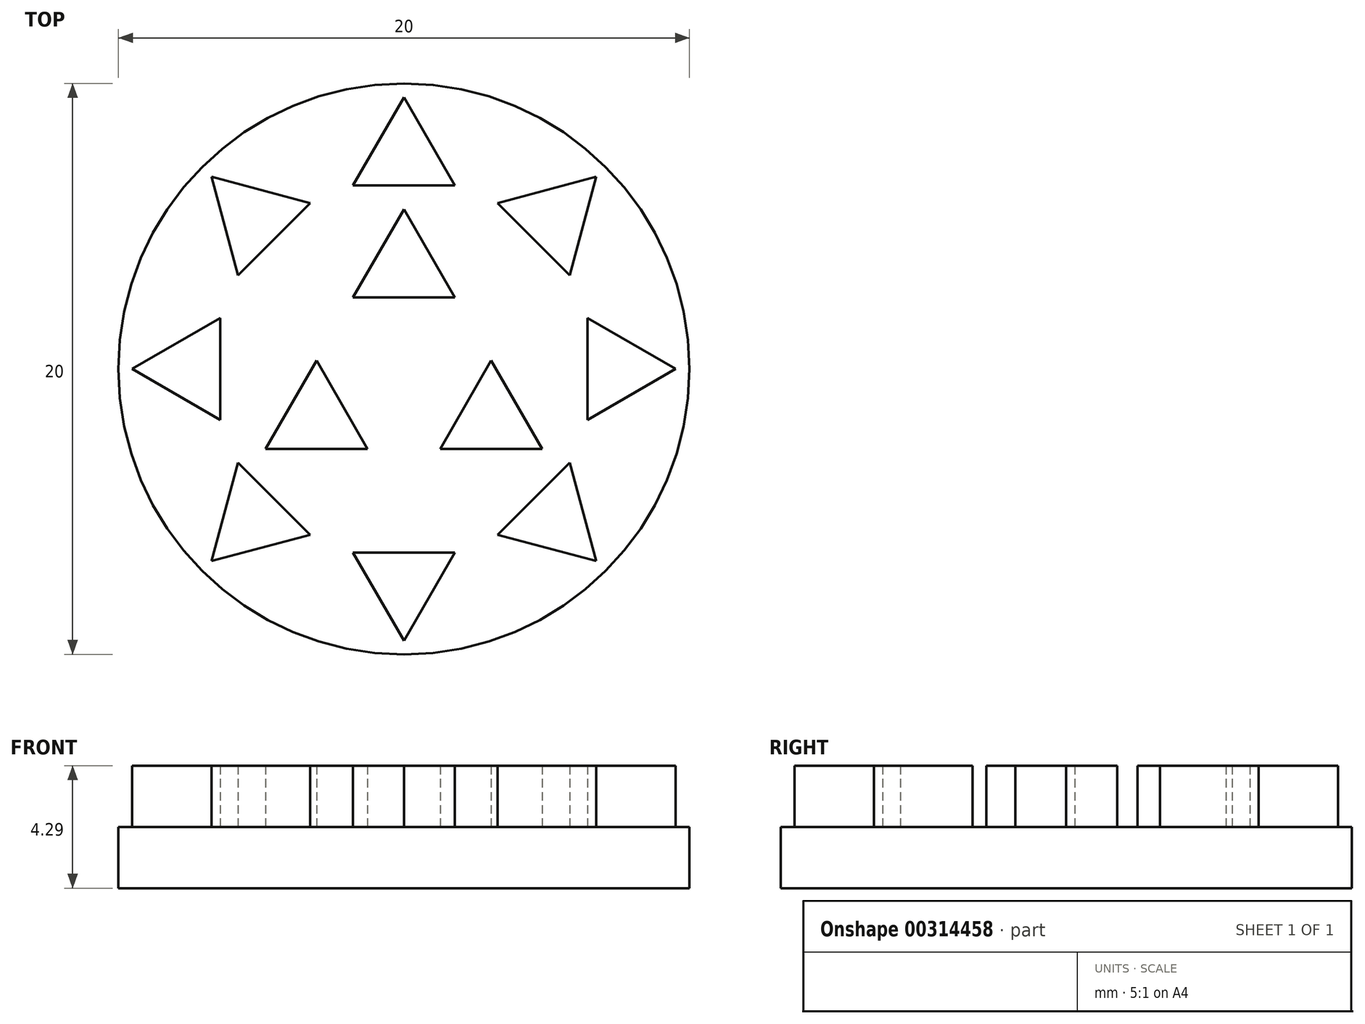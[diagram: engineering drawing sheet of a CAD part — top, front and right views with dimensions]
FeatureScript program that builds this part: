
annotation { "Feature Type Name" : "Feature", "Feature Type Description" : "" }
export const myFeature = defineFeature(function(context is Context, id is Id, definition is map)
    precondition{}
    {
        {
            var Q0;
            Q0=qCreatedBy(makeId("Top.planeOp"),FACE);
            var sketch = newSketch(context, id + "F0", { "sketchPlane" : qUnion([Q0])});
            skCircle(sketch, "E0", {"center": v(0, 0) * mm, "radius": 14 * mm});
            skSolve(sketch);
        }
        {
            var Q0;
            Q0=makeQuery(id+"F0.imprint","IMPRINT",FACE,{"disambiguationData":[TD([[makeQuery(id+"F0.imprint","IMPRINT",EDGE,{"derivedFrom":sQuery(id+"F0.wireOp",EDGE,"E0")}),1.0]])]});
            var Q1;
            Q1 = qSketchRegion(id + "F2", true);
            extrude(context, id + "F1", {"entities" : qUnion([Q0, Q1]), "depth" : 3 * mm});
        }
        {
            var Q0;
            Q0=makeQuery(id+"F1.opExtrude","CAP_FACE",FACE,{"disambiguationData":[OSD([sQuery(id+"F0.wireOp",EDGE,"E0")])],"isStart":false});
            var sketch = newSketch(context, id + "F2", { "sketchPlane" : qUnion([Q0])});
            skCircle(sketch, "E1.cCircle", {"center": v(0, 4.94) * mm, "radius": 1.44 * mm, "construction": true});
            skLineSegment(sketch, "E1.0", {"start": v(2.5, 3.5) * mm, "end": v(-2.5, 3.5) * mm});
            skLineSegment(sketch, "E1.1", {"start": v(-2.5, 3.5) * mm, "end": v(0, 7.83) * mm});
            skLineSegment(sketch, "E1.2", {"start": v(0, 7.83) * mm, "end": v(2.5, 3.5) * mm});
            skPoint(sketch, "E1.0.midPoint", {"position": v(0, 3.5) * mm});
            skCircle(sketch, "E2", {"center": v(0, 0) * mm, "radius": 3.5 * mm});
            skLineSegment(sketch, "E3.1.0", {"start": v(-4.28, 0.42) * mm, "end": v(-1.78, -3.92) * mm});
            skLineSegment(sketch, "E3.1.1", {"start": v(-6.78, -3.92) * mm, "end": v(-4.28, 0.42) * mm});
            skLineSegment(sketch, "E3.1.2", {"start": v(-1.78, -3.92) * mm, "end": v(-6.78, -3.92) * mm});
            skCircle(sketch, "E3.1.3", {"center": v(-4.28, -2.47) * mm, "radius": 1.44 * mm, "construction": true});
            skLineSegment(sketch, "E3.2.0", {"start": v(1.78, -3.92) * mm, "end": v(4.28, 0.42) * mm});
            skLineSegment(sketch, "E3.2.1", {"start": v(6.78, -3.92) * mm, "end": v(1.78, -3.92) * mm});
            skLineSegment(sketch, "E3.2.2", {"start": v(4.28, 0.42) * mm, "end": v(6.78, -3.92) * mm});
            skCircle(sketch, "E3.2.3", {"center": v(4.28, -2.47) * mm, "radius": 1.44 * mm, "construction": true});
            skCircle(sketch, "E4.cCircle", {"center": v(0, 10.44) * mm, "radius": 1.44 * mm, "construction": true});
            skLineSegment(sketch, "E4.0", {"start": v(2.5, 9) * mm, "end": v(-2.5, 9) * mm});
            skLineSegment(sketch, "E4.1", {"start": v(-2.5, 9) * mm, "end": v(0, 13.33) * mm});
            skLineSegment(sketch, "E4.2", {"start": v(0, 13.33) * mm, "end": v(2.5, 9) * mm});
            skPoint(sketch, "E4.0.midPoint", {"position": v(0, 9) * mm});
            skCircle(sketch, "E5", {"center": v(0, 0) * mm, "radius": 9 * mm});
            skLineSegment(sketch, "E6.1.0", {"start": v(-4.6, 8.13) * mm, "end": v(-8.13, 4.6) * mm});
            skLineSegment(sketch, "E6.1.1", {"start": v(-9.43, 9.43) * mm, "end": v(-4.6, 8.13) * mm});
            skLineSegment(sketch, "E6.1.2", {"start": v(-8.13, 4.6) * mm, "end": v(-9.43, 9.43) * mm});
            skCircle(sketch, "E6.1.3", {"center": v(-7.38, 7.38) * mm, "radius": 1.44 * mm, "construction": true});
            skLineSegment(sketch, "E6.2.0", {"start": v(-9, 2.5) * mm, "end": v(-9, -2.5) * mm});
            skLineSegment(sketch, "E6.2.1", {"start": v(-13.33, 0) * mm, "end": v(-9, 2.5) * mm});
            skLineSegment(sketch, "E6.2.2", {"start": v(-9, -2.5) * mm, "end": v(-13.33, 0) * mm});
            skCircle(sketch, "E6.2.3", {"center": v(-10.44, 0) * mm, "radius": 1.44 * mm, "construction": true});
            skLineSegment(sketch, "E7.2.3.0", {"start": v(-8.13, -4.6) * mm, "end": v(-4.6, -8.13) * mm});
            skLineSegment(sketch, "E7.3.3.0", {"start": v(-9.43, -9.43) * mm, "end": v(-8.13, -4.6) * mm});
            skLineSegment(sketch, "E7.6.3.0", {"start": v(-4.6, -8.13) * mm, "end": v(-9.43, -9.43) * mm});
            skCircle(sketch, "E7.9.3.0", {"center": v(-7.38, -7.38) * mm, "radius": 1.44 * mm, "construction": true});
            skLineSegment(sketch, "E7.2.4.0", {"start": v(-2.5, -9) * mm, "end": v(2.5, -9) * mm});
            skLineSegment(sketch, "E7.3.4.0", {"start": v(0, -13.33) * mm, "end": v(-2.5, -9) * mm});
            skLineSegment(sketch, "E7.6.4.0", {"start": v(2.5, -9) * mm, "end": v(0, -13.33) * mm});
            skCircle(sketch, "E7.9.4.0", {"center": v(0, -10.44) * mm, "radius": 1.44 * mm, "construction": true});
            skLineSegment(sketch, "E7.2.5.0", {"start": v(4.6, -8.13) * mm, "end": v(8.13, -4.6) * mm});
            skLineSegment(sketch, "E7.3.5.0", {"start": v(9.43, -9.43) * mm, "end": v(4.6, -8.13) * mm});
            skLineSegment(sketch, "E7.6.5.0", {"start": v(8.13, -4.6) * mm, "end": v(9.43, -9.43) * mm});
            skCircle(sketch, "E7.9.5.0", {"center": v(7.38, -7.38) * mm, "radius": 1.44 * mm, "construction": true});
            skLineSegment(sketch, "E7.2.6.0", {"start": v(9, -2.5) * mm, "end": v(9, 2.5) * mm});
            skLineSegment(sketch, "E7.3.6.0", {"start": v(13.33, 0) * mm, "end": v(9, -2.5) * mm});
            skLineSegment(sketch, "E7.6.6.0", {"start": v(9, 2.5) * mm, "end": v(13.33, 0) * mm});
            skCircle(sketch, "E7.9.6.0", {"center": v(10.44, 0) * mm, "radius": 1.44 * mm, "construction": true});
            skLineSegment(sketch, "E7.2.7.0", {"start": v(8.13, 4.6) * mm, "end": v(4.6, 8.13) * mm});
            skLineSegment(sketch, "E7.3.7.0", {"start": v(9.43, 9.43) * mm, "end": v(8.13, 4.6) * mm});
            skLineSegment(sketch, "E7.6.7.0", {"start": v(4.6, 8.13) * mm, "end": v(9.43, 9.43) * mm});
            skCircle(sketch, "E7.9.7.0", {"center": v(7.38, 7.38) * mm, "radius": 1.44 * mm, "construction": true});
            skPoint(sketch, "E8", {"position": v(6.36, 6.36) * mm});
            skPoint(sketch, "E9", {"position": v(9, 0) * mm});
            skPoint(sketch, "E10", {"position": v(6.36, -6.36) * mm});
            skPoint(sketch, "E11", {"position": v(0, -9) * mm});
            skPoint(sketch, "E12", {"position": v(-6.36, -6.36) * mm});
            skPoint(sketch, "E13", {"position": v(-9, 0) * mm});
            skPoint(sketch, "E14", {"position": v(-6.36, 6.36) * mm});
            skPoint(sketch, "E15", {"position": v(3.03, -1.75) * mm});
            skPoint(sketch, "E16", {"position": v(-3.03, -1.75) * mm});
            skSolve(sketch);
        }
        {
            var Q0;
            {var subQ3=sQuery(id+"F2.wireOp",EDGE,"8b3eb6cf-7dbc-4c96-a035-3d80c259cfac.1");Q0=makeQuery(id+"F2.imprint","IMPRINT",FACE,{"disambiguationData":[TD([[makeQuery(id+"F2.imprint","IMPRINT",EDGE,{"derivedFrom":subQ3}),-1.0]])]});}
            var Q1;
            {var subQ0=sQuery(id+"F2.wireOp",EDGE,"6c10d993-edd7-4a8d-bda8-a9486d968e1a.5.1");Q1=makeQuery(id+"F2.imprint","IMPRINT",FACE,{"disambiguationData":[TD([[makeQuery(id+"F2.imprint","IMPRINT",EDGE,{"derivedFrom":subQ0}),-1.0]])]});}
            var Q2;
            {var subQ0=sQuery(id+"F2.wireOp",EDGE,"6c10d993-edd7-4a8d-bda8-a9486d968e1a.4.1");Q2=makeQuery(id+"F2.imprint","IMPRINT",FACE,{"disambiguationData":[TD([[makeQuery(id+"F2.imprint","IMPRINT",EDGE,{"derivedFrom":subQ0}),-1.0]])]});}
            var Q3;
            {var subQ0=sQuery(id+"F2.wireOp",EDGE,"6c10d993-edd7-4a8d-bda8-a9486d968e1a.3.1");Q3=makeQuery(id+"F2.imprint","IMPRINT",FACE,{"disambiguationData":[TD([[makeQuery(id+"F2.imprint","IMPRINT",EDGE,{"derivedFrom":subQ0}),-1.0]])]});}
            var Q4;
            {var subQ0=sQuery(id+"F2.wireOp",EDGE,"6c10d993-edd7-4a8d-bda8-a9486d968e1a.2.1");Q4=makeQuery(id+"F2.imprint","IMPRINT",FACE,{"disambiguationData":[TD([[makeQuery(id+"F2.imprint","IMPRINT",EDGE,{"derivedFrom":subQ0}),-1.0]])]});}
            var Q5;
            {var subQ0=sQuery(id+"F2.wireOp",EDGE,"6c10d993-edd7-4a8d-bda8-a9486d968e1a.1.1");Q5=makeQuery(id+"F2.imprint","IMPRINT",FACE,{"disambiguationData":[TD([[makeQuery(id+"F2.imprint","IMPRINT",EDGE,{"derivedFrom":subQ0}),-1.0]])]});}
            var Q6;
            {var subQ0=sQuery(id+"F2.wireOp",EDGE,"947e9cf8-dde9-4160-9a07-f35e782527b7.3.7.0");Q6=makeQuery(id+"F2.imprint","IMPRINT",FACE,{"disambiguationData":[TD([[makeQuery(id+"F2.imprint","IMPRINT",EDGE,{"derivedFrom":subQ0}),-1.0]])]});}
            var Q7;
            {var subQ0=sQuery(id+"F2.wireOp",EDGE,"947e9cf8-dde9-4160-9a07-f35e782527b7.3.6.0");Q7=makeQuery(id+"F2.imprint","IMPRINT",FACE,{"disambiguationData":[TD([[makeQuery(id+"F2.imprint","IMPRINT",EDGE,{"derivedFrom":subQ0}),-1.0]])]});}
            var Q8;
            {var subQ0=sQuery(id+"F2.wireOp",EDGE,"947e9cf8-dde9-4160-9a07-f35e782527b7.11.7.0");Q8=makeQuery(id+"F2.imprint","IMPRINT",FACE,{"disambiguationData":[TD([[makeQuery(id+"F2.imprint","IMPRINT",EDGE,{"derivedFrom":subQ0}),-1.0]])]});}
            var Q9;
            {var subQ0=sQuery(id+"F2.wireOp",EDGE,"E1.1");Q9=makeQuery(id+"F2.imprint","IMPRINT",FACE,{"disambiguationData":[TD([[makeQuery(id+"F2.imprint","IMPRINT",EDGE,{"derivedFrom":subQ0}),-1.0]])]});}
            var Q10;
            {var subQ0=sQuery(id+"F2.wireOp",EDGE,"E1.2");Q10=makeQuery(id+"F2.imprint","IMPRINT",FACE,{"disambiguationData":[TD([[makeQuery(id+"F2.imprint","IMPRINT",EDGE,{"derivedFrom":subQ0}),-1.0]])]});}
            var Q11;
            {var subQ0=sQuery(id+"F2.wireOp",EDGE,"E3.1.1");Q11=makeQuery(id+"F2.imprint","IMPRINT",FACE,{"disambiguationData":[TD([[makeQuery(id+"F2.imprint","IMPRINT",EDGE,{"derivedFrom":subQ0}),-1.0]])]});}
            var Q12;
            {var subQ0=sQuery(id+"F2.wireOp",EDGE,"E3.2.1");Q12=makeQuery(id+"F2.imprint","IMPRINT",FACE,{"disambiguationData":[TD([[makeQuery(id+"F2.imprint","IMPRINT",EDGE,{"derivedFrom":subQ0}),-1.0]])]});}
            var Q13;
            {var subQ0=sQuery(id+"F2.wireOp",EDGE,"78a639ae-5dbe-4d62-8846-17a8c4bbea7f.3.3.0");Q13=makeQuery(id+"F2.imprint","IMPRINT",FACE,{"disambiguationData":[TD([[makeQuery(id+"F2.imprint","IMPRINT",EDGE,{"derivedFrom":subQ0}),-1.0]])]});}
            var Q14;
            {var subQ0=sQuery(id+"F2.wireOp",EDGE,"E6.1.1");Q14=makeQuery(id+"F2.imprint","IMPRINT",FACE,{"disambiguationData":[TD([[makeQuery(id+"F2.imprint","IMPRINT",EDGE,{"derivedFrom":subQ0}),-1.0]])]});}
            var Q15;
            {var subQ3=sQuery(id+"F2.wireOp",EDGE,"E4.1");Q15=makeQuery(id+"F2.imprint","IMPRINT",FACE,{"disambiguationData":[TD([[makeQuery(id+"F2.imprint","IMPRINT",EDGE,{"derivedFrom":subQ3}),-1.0]])]});}
            var Q16;
            {var subQ0=sQuery(id+"F2.wireOp",EDGE,"E7.3.7.0");Q16=makeQuery(id+"F2.imprint","IMPRINT",FACE,{"disambiguationData":[TD([[makeQuery(id+"F2.imprint","IMPRINT",EDGE,{"derivedFrom":subQ0}),-1.0]])]});}
            var Q17;
            {var subQ0=sQuery(id+"F2.wireOp",EDGE,"E7.3.6.0");Q17=makeQuery(id+"F2.imprint","IMPRINT",FACE,{"disambiguationData":[TD([[makeQuery(id+"F2.imprint","IMPRINT",EDGE,{"derivedFrom":subQ0}),-1.0]])]});}
            var Q18;
            {var subQ0=sQuery(id+"F2.wireOp",EDGE,"E7.3.5.0");Q18=makeQuery(id+"F2.imprint","IMPRINT",FACE,{"disambiguationData":[TD([[makeQuery(id+"F2.imprint","IMPRINT",EDGE,{"derivedFrom":subQ0}),-1.0]])]});}
            var Q19;
            {var subQ0=sQuery(id+"F2.wireOp",EDGE,"E7.3.4.0");Q19=makeQuery(id+"F2.imprint","IMPRINT",FACE,{"disambiguationData":[TD([[makeQuery(id+"F2.imprint","IMPRINT",EDGE,{"derivedFrom":subQ0}),-1.0]])]});}
            var Q20;
            {var subQ0=sQuery(id+"F2.wireOp",EDGE,"E7.3.3.0");Q20=makeQuery(id+"F2.imprint","IMPRINT",FACE,{"disambiguationData":[TD([[makeQuery(id+"F2.imprint","IMPRINT",EDGE,{"derivedFrom":subQ0}),-1.0]])]});}
            var Q21;
            {var subQ0=sQuery(id+"F2.wireOp",EDGE,"E6.2.1");Q21=makeQuery(id+"F2.imprint","IMPRINT",FACE,{"disambiguationData":[TD([[makeQuery(id+"F2.imprint","IMPRINT",EDGE,{"derivedFrom":subQ0}),-1.0]])]});}
            extrude(context, id + "F3", {"entities" : qUnion([Q0, Q1, Q2, Q3, Q4, Q5, Q6, Q7, Q8, Q9, Q10, Q11, Q12, Q13, Q14, Q15, Q16, Q17, Q18, Q19, Q20, Q21]), "operationType" : NewBodyOperationType.ADD, "depth" : 3 * mm});
        }
        {
            var Q0;
            Q0=makeQuery(id+"F1.opExtrude","SWEPT_BODY",BODY,{"disambiguationData":[OSD([sQuery(id+"F0.wireOp",EDGE,"E0")])]});
            var Q1;
            Q1=qCreatedBy(makeId("Origin.pointOp"),VERTEX);
            transform(context, id + "F4", {"entities" : qUnion([Q0]), "transformType" : TransformType.SCALE_UNIFORMLY, "scale" : 0.71, "scalePoint" : qUnion([Q1]), "makeCopy" : false});
        }
    });
